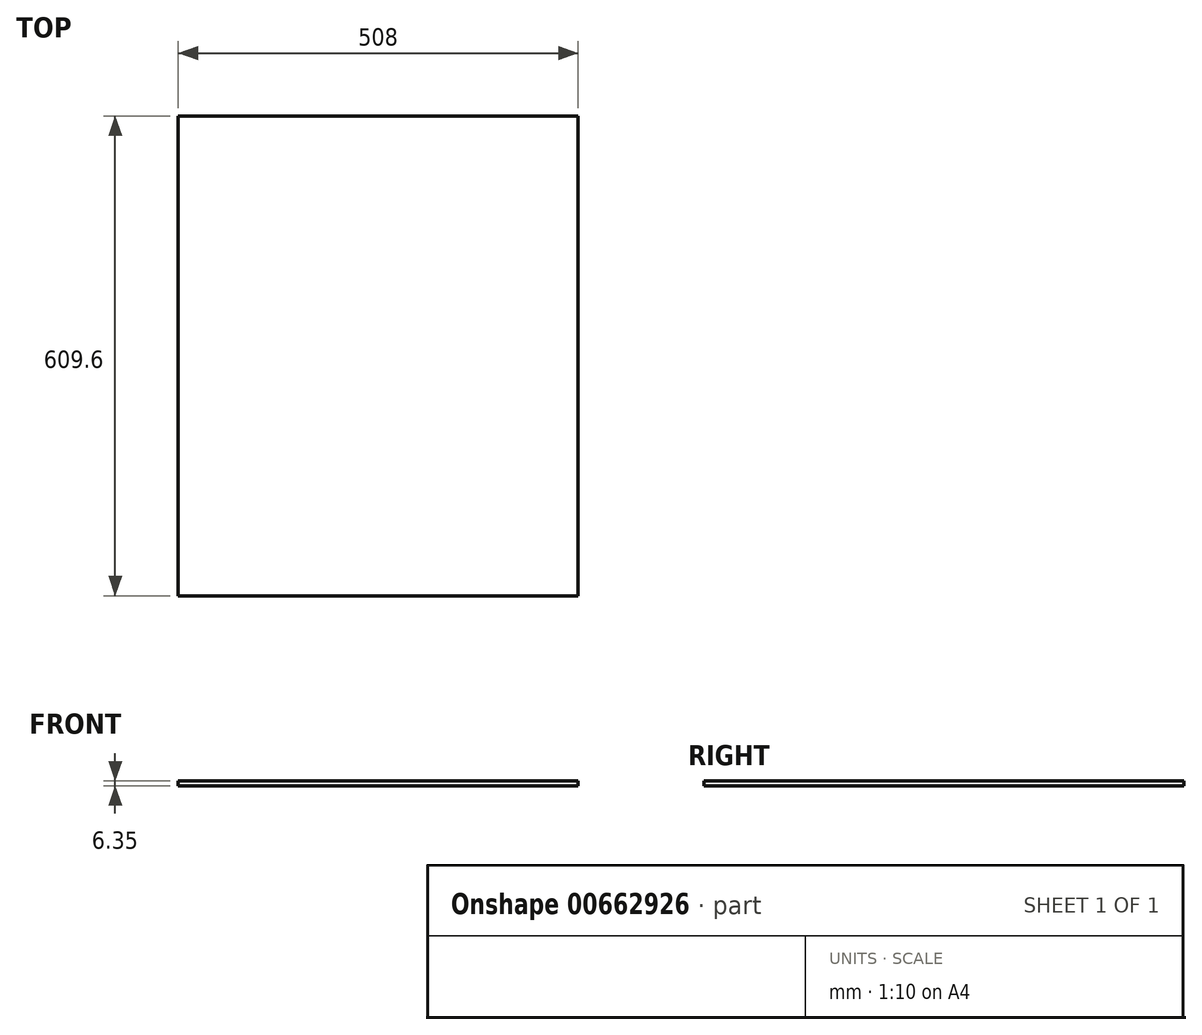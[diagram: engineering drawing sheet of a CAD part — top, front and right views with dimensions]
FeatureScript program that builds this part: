
annotation { "Feature Type Name" : "Feature", "Feature Type Description" : "" }
export const myFeature = defineFeature(function(context is Context, id is Id, definition is map)
    precondition{}
    {
        {
            var Q0;
            Q0=qCreatedBy(makeId("Top.planeOp"),FACE);
            var sketch = newSketch(context, id + "F0", { "sketchPlane" : qUnion([Q0])});
            skLineSegment(sketch, "E0.bottom", {"start": v(-460.28, 581.43) * mm, "end": v(47.72, 581.43) * mm});
            skLineSegment(sketch, "E0.top", {"start": v(-460.28, -28.17) * mm, "end": v(47.72, -28.17) * mm});
            skLineSegment(sketch, "E0.left", {"start": v(-460.28, 581.43) * mm, "end": v(-460.28, -28.17) * mm});
            skLineSegment(sketch, "E0.right", {"start": v(47.72, 581.43) * mm, "end": v(47.72, -28.17) * mm});
            skSolve(sketch);
        }
        {
            var Q0;
            Q0 = qSketchRegion(id + "F0", true);
            extrude(context, id + "F1", {"entities" : qUnion([Q0]), "depth" : 6.35 * mm, "offsetDistance" : 25.4 * mm});
        }
    });
